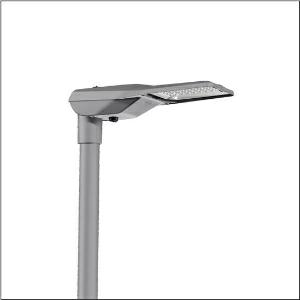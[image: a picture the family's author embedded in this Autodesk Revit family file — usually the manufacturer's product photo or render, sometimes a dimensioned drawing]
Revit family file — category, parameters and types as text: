
# Revit family: streetlight_sl_21_iq_mini___p1_0a_5xe2a31y08hb_fafd
name_source: partatom
category: Lighting Fixtures
units: mm (PartAtom-declared; Revit-internal decimal feet)

## family parameters
Cut with Voids When Loaded = No
Host = Face
Light Source = No
Part Type = Normal
Room Calculation Point = No
Round Connector Dimension = Use Diameter
Shared = No

## types (1)
- --- (1 x LED, 9750 lm, 71 W, 3000K)
    Apparent Load = 71 VA
    CIE Flux Codes = 21 50 90 100 100
    Color Rendering = 70
    Color Temperature = 3000K
    Default Elevation = 1800 mm
    Description = Streetlight SL 21 iQ mini, mast luminaire, primary light control with lens, of PMMA, primary optical cover: cover, of toughened safety glass, transparent, light distribution: P1.0a, light emission: direct distribution, primary light characteristic: asymmetric, installation type: post-top, side-entry, LED, High Power LED, rated luminous flux: 9.750lm, luminous efficacy: 137lm/W, light colour: 730, colour temperature: 3000K, control: presetting dimming logarithmic, Street-Remote, Auto-Match, Temp-Guard, Lumen-Switch, Night-Set, Smart-Wire, Light-Fading, Desk-Remote (wireless, voltage-free reading and setting of iQ features in the workshop via application-optimized NFC function/RFID function), optimised constant luminous flux control (CLO 2.0), mains connection: 220..240V, AC, 50/60Hz, start of lifetime: 71W, end of service life: 75W, reduction: 30W, luminaire housing, of diecast aluminium, powder-coated, Siteco® metallic grey (DB 702S), corrosivity category C5 mid according to DIN EN ISO 12944, please order mast flange separately, inclination adjustable: 0°, 5°, 10°, 15°, sealing non-destructively replaceable, multi-level sealing system, length: 628mm, width: 235mm, height: 110mm, mast flange for spigot size: 42mm (side-entry): 5XC10008XM4, 60/48mm (side-entry/post-top): 5XC10108XM2, 76/60mm (side-entry/post-top): 5XC10108XM1, Smart Interface below and above, protection rating (complete): IP66, insulation class (complete): insulation class II (safety insulation), certification: CE, ENEC, ENEC+, VDE, impact resistance: IK09, permissible operating ambient temperature for outdoor applications: -40..+50°C, standard-compliant lighting for roads and squares, packaging unit: 1 piece

Light Distribution: P1.0a
    Height = 110 mm
    Lamp = 1 x LED
    Lamp Light Flux = 9750 lm
    Lamp Power = 71 W
    Lamp count = 1
    Length = 625 mm
    Luminous efficacy = 137 lm/W
    Manufacturer = Siteco
    ModVariant = No
    Model = 5XE2A31Y08HB
    Number of Poles = 1
    OnlyDefault = Yes
    Power Factor = 1
    Product Name = Streetlight SL 21 iQ mini | P1.0a
    Product group = mast luminaire | pylon top
    ProductGroupID = 6100
    Protection Class = Protection class II
    Protection Degree = IP 66
    RLX_Detail_Level = 1
    RLX_Emergency_Light_Flux = 0 lm
    RLX_Emergency_Type = 0
    RLX_Emergency_Type_DB = No
    RlxData = <blob elided: 103673 chars, md5=37ffe735>
    Socket = socket
    Standby Power = 0 W
    System Light Flux = 9750 lm
    System Power = 71 W
    Type Comments = factory setting: luminous flux: 100 % | dim-lin: 254 | 716 mA
    Type Image = l_1003514.jpg
    URL = http://relux.com
    VarID = @adj_043539
    Voltage = 0 V
    Weight = 0.00 kg
    Width = 234 mm

## geometry (parser evidence)
native form markers: Blend x4, Sweep x11
no freeform markers — native parametric forms only
